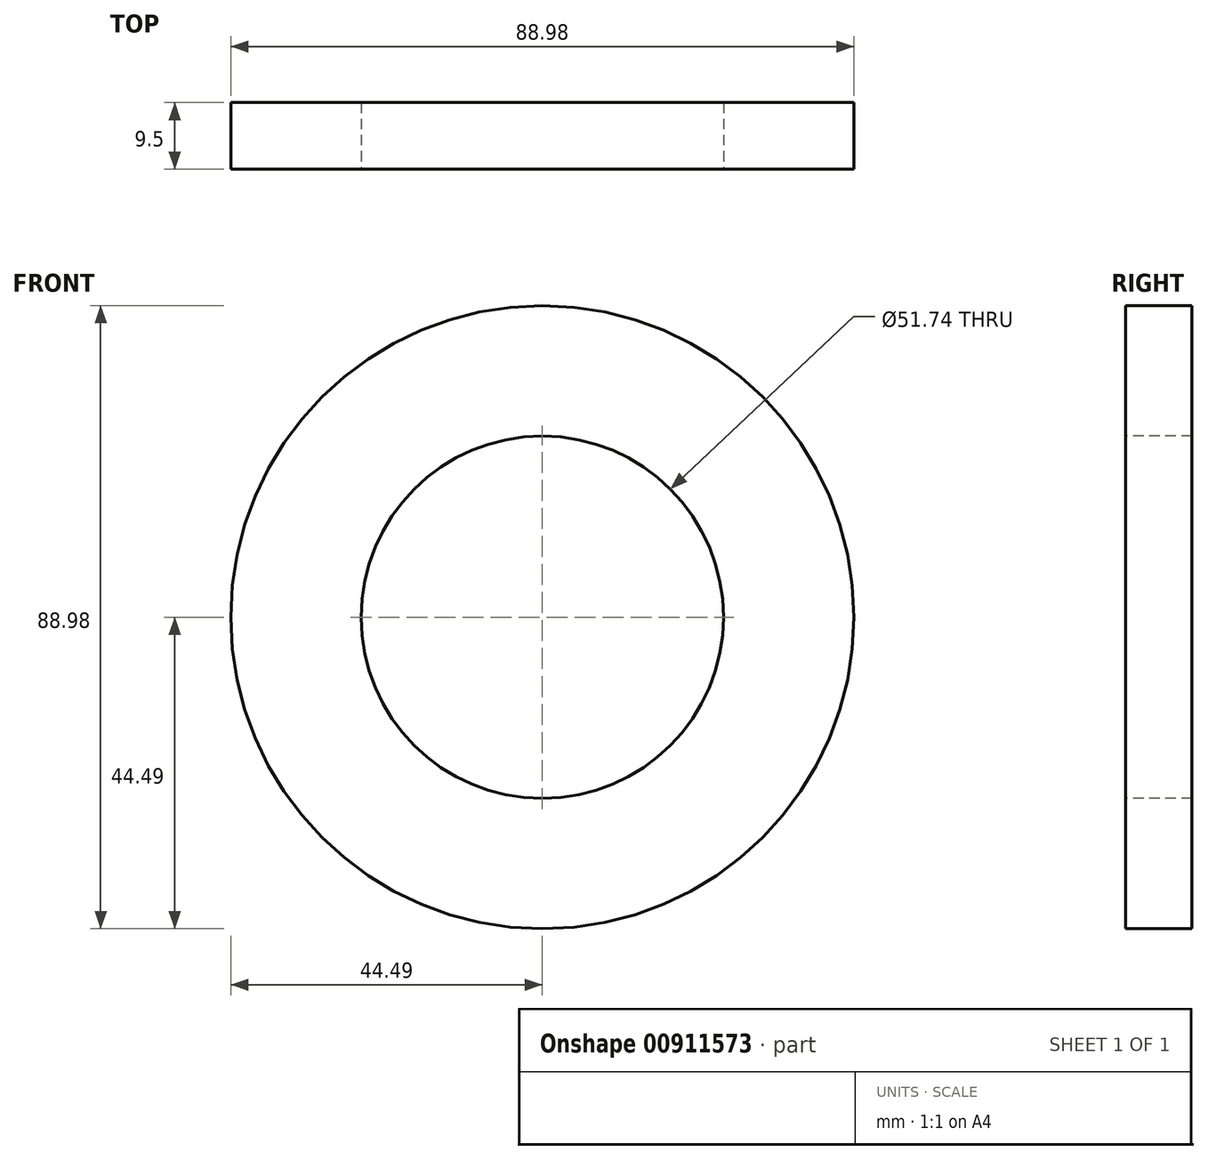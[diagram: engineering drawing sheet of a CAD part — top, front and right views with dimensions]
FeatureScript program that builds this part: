
annotation { "Feature Type Name" : "Feature", "Feature Type Description" : "" }
export const myFeature = defineFeature(function(context is Context, id is Id, definition is map)
    precondition{}
    {
        {
            var Q0;
            Q0=qCreatedBy(makeId("Front.planeOp"),FACE);
            var sketch = newSketch(context, id + "F0", { "sketchPlane" : qUnion([Q0])});
            skCircle(sketch, "E0", {"center": v(0, 0) * mm, "radius": 44.49 * mm});
            skSolve(sketch);
        }
        {
            var Q0;
            Q0=makeQuery(id+"F0.imprint","IMPRINT",FACE,{"disambiguationData":[TD([[makeQuery(id+"F0.imprint","IMPRINT",EDGE,{"derivedFrom":sQuery(id+"F0.wireOp",EDGE,"E0")}),1.0]])]});
            extrude(context, id + "F1", {"entities" : qUnion([Q0]), "oppositeDirection" : true, "depth" : 9.5 * mm, "offsetDistance" : 25 * mm});
        }
        {
            var Q0;
            Q0=qCreatedBy(makeId("Front.planeOp"),FACE);
            var sketch = newSketch(context, id + "F2", { "sketchPlane" : qUnion([Q0])});
            skCircle(sketch, "E1", {"center": v(0, 0) * mm, "radius": 25.81 * mm});
            skSolve(sketch);
        }
        {
            var Q0;
            Q0=qCreatedBy(makeId("Front.planeOp"),FACE);
            var sketch = newSketch(context, id + "F3", { "sketchPlane" : qUnion([Q0])});
            skSolve(sketch);
        }
        {
            var Q0;
            Q0 = qSketchRegion(id + "F3", true);
            var Q1;
            Q1=makeQuery(id+"F2.imprint","IMPRINT",FACE,{"disambiguationData":[TD([[makeQuery(id+"F2.imprint","IMPRINT",EDGE,{"derivedFrom":sQuery(id+"F2.wireOp",EDGE,"E1")}),1.0]])]});
            extrude(context, id + "F4", {"entities" : qUnion([Q0, Q1]), "operationType" : NewBodyOperationType.ADD, "oppositeDirection" : true, "depth" : 8.7 * mm, "offsetDistance" : 25 * mm});
        }
        {
            var Q0;
            Q0=qCreatedBy(makeId("Front.planeOp"),FACE);
            var sketch = newSketch(context, id + "F5", { "sketchPlane" : qUnion([Q0])});
            skCircle(sketch, "E2", {"center": v(0, 0) * mm, "radius": 25.87 * mm});
            skSolve(sketch);
        }
        {
            var Q0;
            Q0=makeQuery(id+"F5.imprint","IMPRINT",FACE,{"disambiguationData":[TD([[makeQuery(id+"F5.imprint","IMPRINT",EDGE,{"derivedFrom":sQuery(id+"F5.wireOp",EDGE,"E2")}),1.0]])]});
            extrude(context, id + "F6", {"entities" : qUnion([Q0]), "operationType" : NewBodyOperationType.REMOVE, "oppositeDirection" : true, "depth" : 25 * mm, "offsetDistance" : 25 * mm});
        }
    });
